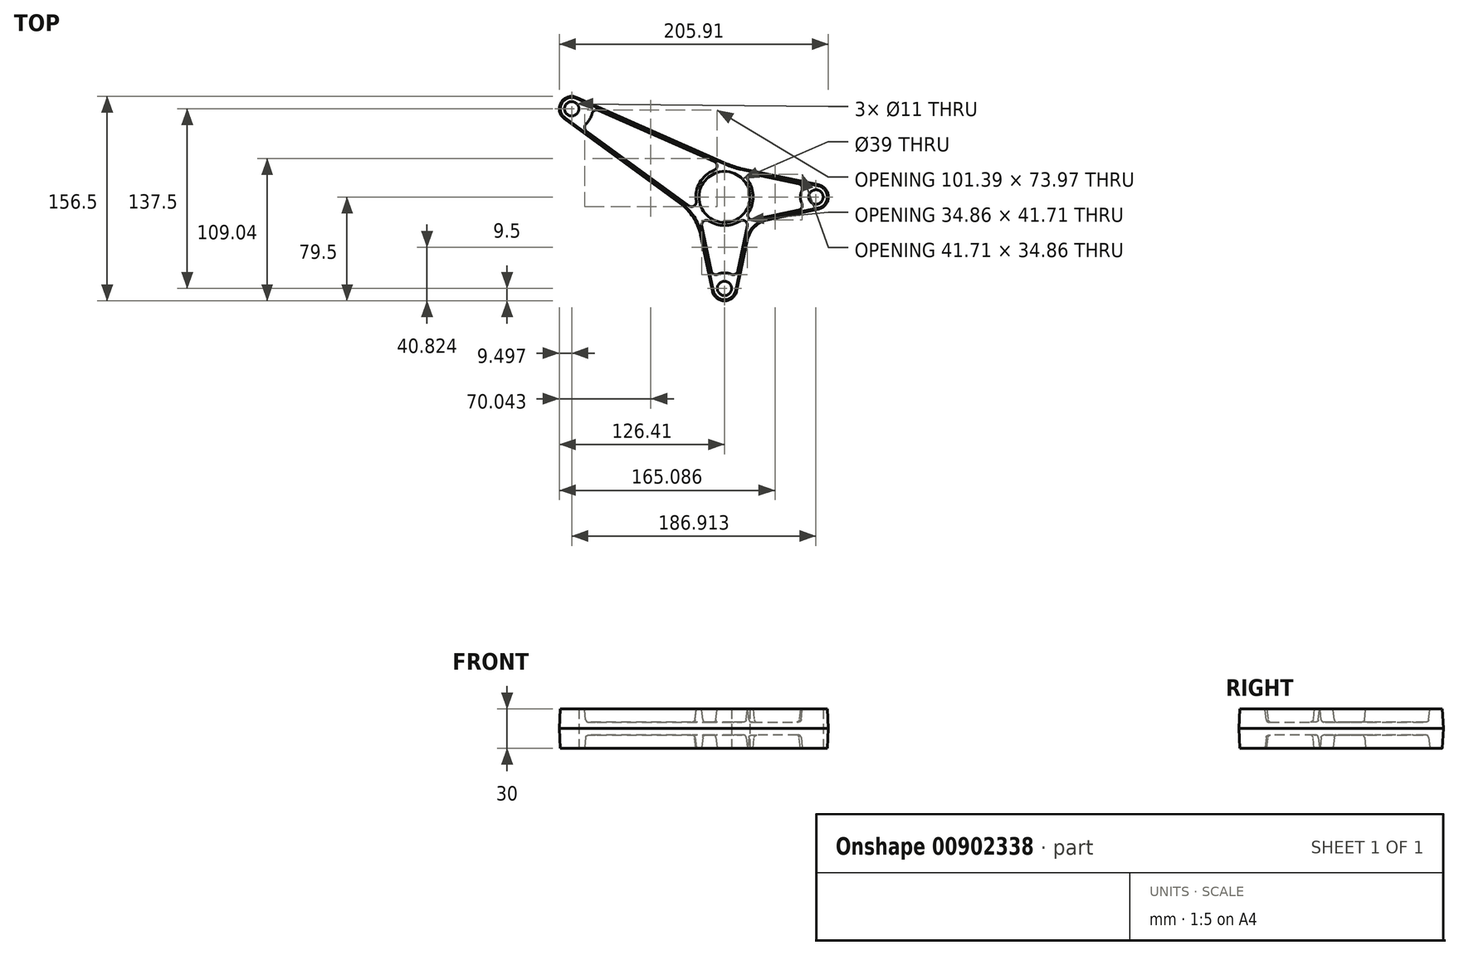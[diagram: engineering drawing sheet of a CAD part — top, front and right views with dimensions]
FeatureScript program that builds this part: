
annotation { "Feature Type Name" : "Feature", "Feature Type Description" : "" }
export const myFeature = defineFeature(function(context is Context, id is Id, definition is map)
    precondition{}
    {
        {
            var Q0;
            Q0=qCreatedBy(makeId("Top.planeOp"),FACE);
            var sketch = newSketch(context, id + "F0", { "sketchPlane" : qUnion([Q0])});
            skLineSegment(sketch, "E0", {"start": v(0, 0) * mm, "end": v(-133.76, 77.23) * mm, "construction": true});
            skLineSegment(sketch, "E1", {"start": v(0, 0) * mm, "end": v(0, -139.43) * mm, "construction": true});
            skCircle(sketch, "E2", {"center": v(0, 0) * mm, "radius": 19.5 * mm});
            skLineSegment(sketch, "E3", {"start": v(0, 0) * mm, "end": v(94.38, 0) * mm, "construction": true});
            skArc(sketch, "E4", {"start": v(0, -70) * mm, "mid": v(49.5, -49.5) * mm, "end": v(70, 0) * mm, "construction": true});
            skCircle(sketch, "E5", {"center": v(0, -70) * mm, "radius": 5.5 * mm});
            skArc(sketch, "E6", {"start": v(-9.3, -71.97) * mm, "mid": v(0, -79.5) * mm, "end": v(9.3, -71.97) * mm});
            skCircle(sketch, "E7", {"center": v(70, 0) * mm, "radius": 5.5 * mm});
            skArc(sketch, "E8", {"start": v(71.97, -9.3) * mm, "mid": v(79.5, 0) * mm, "end": v(71.97, 9.3) * mm});
            skLineSegment(sketch, "E9", {"start": v(71.97, -9.3) * mm, "end": v(32.97, -17.55) * mm});
            skLineSegment(sketch, "E10", {"start": v(9.3, -71.97) * mm, "end": v(17.55, -32.97) * mm});
            skArc(sketch, "E11.trimOffspring", {"start": v(32.97, -17.55) * mm, "mid": v(22.97, -22.97) * mm, "end": v(17.55, -32.97) * mm});
            skArc(sketch, "E12", {"start": v(57.77, 5.7) * mm, "mid": v(56.5, 0) * mm, "end": v(57.77, -5.7) * mm});
            skArc(sketch, "E13", {"start": v(5.7, -57.77) * mm, "mid": v(0, -56.5) * mm, "end": v(-5.7, -57.77) * mm});
            skArc(sketch, "E14", {"start": v(-113.07, 76.19) * mm, "mid": v(-125.14, 72.25) * mm, "end": v(-122.52, 59.83) * mm});
            skCircle(sketch, "E15", {"center": v(-116.91, 67.5) * mm, "radius": 5.5 * mm});
            skArc(sketch, "E16", {"start": v(-18.4, -28.93) * mm, "mid": v(-23.95, -15.5) * mm, "end": v(-33.93, -4.92) * mm});
            skLineSegment(sketch, "E17", {"start": v(-9.3, -71.97) * mm, "end": v(-18.4, -28.93) * mm});
            skLineSegment(sketch, "E18", {"start": v(-122.52, 59.83) * mm, "end": v(-33.93, -4.92) * mm});
            skArc(sketch, "E19", {"start": v(2.66, 25.06) * mm, "mid": v(7.5, 23.22) * mm, "end": v(12.5, 21.88) * mm});
            skLineSegment(sketch, "E20", {"start": v(71.97, 9.3) * mm, "end": v(12.5, 21.88) * mm});
            skLineSegment(sketch, "E21", {"start": v(-113.07, 76.19) * mm, "end": v(2.66, 25.06) * mm});
            skLineSegment(sketch, "E22.0", {"start": v(56.37, 8.5) * mm, "end": v(21.81, 15.82) * mm});
            skLineSegment(sketch, "E23.0", {"start": v(56.37, -8.5) * mm, "end": v(21.81, -15.82) * mm});
            skArc(sketch, "E24.0", {"start": v(19.72, -12.78) * mm, "mid": v(23.5, 0) * mm, "end": v(19.72, 12.78) * mm});
            skArc(sketch, "E25.filletArc", {"start": v(57.77, 5.7) * mm, "mid": v(57.74, 7.44) * mm, "end": v(56.37, 8.5) * mm});
            skArc(sketch, "E26.filletArc", {"start": v(56.37, -8.5) * mm, "mid": v(57.74, -7.44) * mm, "end": v(57.77, -5.7) * mm});
            skArc(sketch, "E27.filletArc", {"start": v(19.72, -12.78) * mm, "mid": v(19.75, -15) * mm, "end": v(21.81, -15.82) * mm});
            skArc(sketch, "E28.trimOffspring", {"start": v(-12.78, -19.72) * mm, "mid": v(0, -23.5) * mm, "end": v(12.78, -19.72) * mm});
            skArc(sketch, "E29.filletArc", {"start": v(21.81, 15.82) * mm, "mid": v(19.75, 15) * mm, "end": v(19.72, 12.78) * mm});
            skArc(sketch, "E30.filletArc", {"start": v(15.82, -21.81) * mm, "mid": v(15, -19.75) * mm, "end": v(12.78, -19.72) * mm});
            skLineSegment(sketch, "E31.trimOffspring", {"start": v(8.5, -56.37) * mm, "end": v(15.82, -21.81) * mm});
            skPoint(sketch, "E32.visualSharp", {"position": v(7.93, -59.08) * mm});
            skArc(sketch, "E32.filletArc", {"start": v(5.7, -57.77) * mm, "mid": v(7.44, -57.74) * mm, "end": v(8.5, -56.37) * mm});
            skLineSegment(sketch, "E33.0", {"start": v(-8.5, -56.37) * mm, "end": v(-15.82, -21.81) * mm});
            skArc(sketch, "E34.filletArc", {"start": v(-12.78, -19.72) * mm, "mid": v(-15, -19.75) * mm, "end": v(-15.82, -21.81) * mm});
            skPoint(sketch, "E35.visualSharp", {"position": v(-7.93, -59.08) * mm});
            skArc(sketch, "E35.filletArc", {"start": v(-8.5, -56.37) * mm, "mid": v(-7.44, -57.74) * mm, "end": v(-5.7, -57.77) * mm});
            skArc(sketch, "E36.trimOffspring", {"start": v(-116.91, 67.5) * mm, "mid": v(-116.91, -67.5) * mm, "end": v(0, -135) * mm, "construction": true});
            skLineSegment(sketch, "E37.0", {"start": v(-97.14, 64.78) * mm, "end": v(-8.44, 25.6) * mm});
            skArc(sketch, "E38.0", {"start": v(-104.87, 54.8) * mm, "mid": v(-101.76, 58.75) * mm, "end": v(-99.9, 63.42) * mm});
            skArc(sketch, "E39.0", {"start": v(-8.52, 21.9) * mm, "mid": v(-20.35, 11.75) * mm, "end": v(-23.23, -3.57) * mm});
            skLineSegment(sketch, "E40.trimOffspring", {"start": v(-104.67, 51.74) * mm, "end": v(-26.38, -5.49) * mm});
            skPoint(sketch, "E41.visualSharp", {"position": v(-99.5, 65.82) * mm});
            skArc(sketch, "E41.filletArc", {"start": v(-97.14, 64.78) * mm, "mid": v(-98.84, 64.74) * mm, "end": v(-99.9, 63.42) * mm});
            skPoint(sketch, "E42.visualSharp", {"position": v(-106.75, 53.26) * mm});
            skArc(sketch, "E42.filletArc", {"start": v(-104.87, 54.8) * mm, "mid": v(-105.49, 53.23) * mm, "end": v(-104.67, 51.74) * mm});
            skPoint(sketch, "E43.visualSharp", {"position": v(-21.76, -8.86) * mm});
            skArc(sketch, "E43.filletArc", {"start": v(-26.38, -5.49) * mm, "mid": v(-24.17, -5.58) * mm, "end": v(-23.23, -3.57) * mm});
            skPoint(sketch, "E44.visualSharp", {"position": v(-3.2, 23.28) * mm});
            skArc(sketch, "E44.filletArc", {"start": v(-8.52, 21.9) * mm, "mid": v(-7.25, 23.72) * mm, "end": v(-8.44, 25.6) * mm});
            skSolve(sketch);
        }
        {
            var Q0;
            Q0=makeQuery(id+"F0.imprint","IMPRINT",FACE,{"disambiguationData":[TD([[makeQuery(id+"F0.imprint","IMPRINT",EDGE,{"derivedFrom":sQuery(id+"F0.wireOp",EDGE,"E2")}),-1.0]])]});
            var Q1;
            Q1=makeQuery(id+"F0.imprint","IMPRINT",FACE,{"disambiguationData":[TD([[makeQuery(id+"F0.imprint","IMPRINT",EDGE,{"derivedFrom":sQuery(id+"F0.wireOp",EDGE,"E13")}),-1.0]])]});
            var Q2;
            Q2=makeQuery(id+"F0.imprint","IMPRINT",FACE,{"disambiguationData":[TD([[makeQuery(id+"F0.imprint","IMPRINT",EDGE,{"derivedFrom":sQuery(id+"F0.wireOp",EDGE,"E15")}),1.0]])]});
            var Q3;
            Q3=makeQuery(id+"F0.imprint","IMPRINT",FACE,{"disambiguationData":[TD([[makeQuery(id+"F0.imprint","IMPRINT",EDGE,{"derivedFrom":sQuery(id+"F0.wireOp",EDGE,"E37.0")}),-1.0]])]});
            var Q4;
            Q4=makeQuery(id+"F0.imprint","IMPRINT",FACE,{"disambiguationData":[TD([[makeQuery(id+"F0.imprint","IMPRINT",EDGE,{"derivedFrom":sQuery(id+"F0.wireOp",EDGE,"E2")}),1.0]])]});
            var Q5;
            Q5=makeQuery(id+"F0.imprint","IMPRINT",FACE,{"disambiguationData":[TD([[makeQuery(id+"F0.imprint","IMPRINT",EDGE,{"derivedFrom":sQuery(id+"F0.wireOp",EDGE,"E5")}),1.0]])]});
            var Q6;
            Q6=makeQuery(id+"F0.imprint","IMPRINT",FACE,{"disambiguationData":[TD([[makeQuery(id+"F0.imprint","IMPRINT",EDGE,{"derivedFrom":sQuery(id+"F0.wireOp",EDGE,"E12")}),-1.0]])]});
            var Q7;
            Q7=makeQuery(id+"F0.imprint","IMPRINT",FACE,{"disambiguationData":[TD([[makeQuery(id+"F0.imprint","IMPRINT",EDGE,{"derivedFrom":sQuery(id+"F0.wireOp",EDGE,"E7")}),1.0]])]});
            extrude(context, id + "F1", {"entities" : qUnion([Q0, Q1, Q2, Q3, Q4, Q5, Q6, Q7]), "depth" : 15 * mm, "offsetDistance" : 25 * mm, "hasDraft" : true, "draftAngle" : 3 * degree, "draftPullDirection" : true});
        }
        {
            var Q0;
            Q0=makeQuery(id+"F0.imprint","IMPRINT",FACE,{"disambiguationData":[TD([[makeQuery(id+"F0.imprint","IMPRINT",EDGE,{"derivedFrom":sQuery(id+"F0.wireOp",EDGE,"E37.0")}),-1.0]])]});
            var Q1;
            Q1=makeQuery(id+"F0.imprint","IMPRINT",FACE,{"disambiguationData":[TD([[makeQuery(id+"F0.imprint","IMPRINT",EDGE,{"derivedFrom":sQuery(id+"F0.wireOp",EDGE,"E13")}),-1.0]])]});
            var Q2;
            Q2=makeQuery(id+"F0.imprint","IMPRINT",FACE,{"disambiguationData":[TD([[makeQuery(id+"F0.imprint","IMPRINT",EDGE,{"derivedFrom":sQuery(id+"F0.wireOp",EDGE,"E12")}),-1.0]])]});
            extrude(context, id + "F2", {"entities" : qUnion([Q0, Q1, Q2]), "operationType" : NewBodyOperationType.REMOVE, "depth" : 30000 * mm, "offsetDistance" : 25 * mm, "hasDraft" : true, "draftAngle" : 6 * degree, "hasSecondDirection" : true, "secondDirectionOppositeDirection" : true, "secondDirectionDepth" : -5 * mm});
        }
        {
            var Q0;
            Q0=makeQuery(id+"F0.imprint","IMPRINT",FACE,{"disambiguationData":[TD([[makeQuery(id+"F0.imprint","IMPRINT",EDGE,{"derivedFrom":sQuery(id+"F0.wireOp",EDGE,"E15")}),1.0]])]});
            var Q1;
            Q1=makeQuery(id+"F0.imprint","IMPRINT",FACE,{"disambiguationData":[TD([[makeQuery(id+"F0.imprint","IMPRINT",EDGE,{"derivedFrom":sQuery(id+"F0.wireOp",EDGE,"E5")}),1.0]])]});
            var Q2;
            Q2=makeQuery(id+"F0.imprint","IMPRINT",FACE,{"disambiguationData":[TD([[makeQuery(id+"F0.imprint","IMPRINT",EDGE,{"derivedFrom":sQuery(id+"F0.wireOp",EDGE,"E2")}),1.0]])]});
            var Q3;
            Q3=makeQuery(id+"F0.imprint","IMPRINT",FACE,{"disambiguationData":[TD([[makeQuery(id+"F0.imprint","IMPRINT",EDGE,{"derivedFrom":sQuery(id+"F0.wireOp",EDGE,"E7")}),1.0]])]});
            var Q4;
            Q4=makeQuery(id+"F1.opExtrude","CAP_FACE",FACE,{"disambiguationData":[OSD([sQuery(id+"F0.wireOp",EDGE,"E6"),sQuery(id+"F0.wireOp",EDGE,"E8"),sQuery(id+"F0.wireOp",EDGE,"E9"),sQuery(id+"F0.wireOp",EDGE,"E10"),sQuery(id+"F0.wireOp",EDGE,"E11.trimOffspring"),sQuery(id+"F0.wireOp",EDGE,"E14"),sQuery(id+"F0.wireOp",EDGE,"E16"),sQuery(id+"F0.wireOp",EDGE,"E17"),sQuery(id+"F0.wireOp",EDGE,"E18"),sQuery(id+"F0.wireOp",EDGE,"E19"),sQuery(id+"F0.wireOp",EDGE,"E20"),sQuery(id+"F0.wireOp",EDGE,"E21")])],"isStart":false});
            extrude(context, id + "F3", {"entities" : qUnion([Q0, Q1, Q2, Q3]), "operationType" : NewBodyOperationType.REMOVE, "endBound" : BoundingType.UP_TO_SURFACE, "depth" : 25 * mm, "endBoundEntityFace" : qUnion([Q4]), "offsetDistance" : 25 * mm});
        }
        {
            var Q0;
            Q0=makeQuery(id+"F2.boolean.opBoolean","COPY",EDGE,{"derivedFrom":makeQuery(id+"F2.opExtrude","CAP_EDGE",EDGE,{"disambiguationData":[OSD([sQuery(id+"F0.wireOp",EDGE,"E37.0")])],"isStart":true})});
            var Q1;
            Q1=makeQuery(id+"F2.boolean.opBoolean","COPY",EDGE,{"derivedFrom":makeQuery(id+"F2.opExtrude","CAP_EDGE",EDGE,{"disambiguationData":[OSD([sQuery(id+"F0.wireOp",EDGE,"E22.0")])],"isStart":true})});
            var Q2;
            Q2=makeQuery(id+"F2.boolean.opBoolean","COPY",EDGE,{"derivedFrom":makeQuery(id+"F2.opExtrude","CAP_EDGE",EDGE,{"disambiguationData":[OSD([sQuery(id+"F0.wireOp",EDGE,"E28.trimOffspring")])],"isStart":true})});
            fillet(context, id + "F4", {"entities" : qUnion([Q0, Q1, Q2]), "radius" : 2 * mm, "tangentPropagation" : true, "allowEdgeOverflow" : false});
        }
        {
            var Q0;
            Q0=makeQuery(id+"F1.opExtrude","SWEPT_BODY",BODY,{"disambiguationData":[OSD([sQuery(id+"F0.wireOp",EDGE,"E6"),sQuery(id+"F0.wireOp",EDGE,"E8"),sQuery(id+"F0.wireOp",EDGE,"E9"),sQuery(id+"F0.wireOp",EDGE,"E10"),sQuery(id+"F0.wireOp",EDGE,"E11.trimOffspring"),sQuery(id+"F0.wireOp",EDGE,"E14"),sQuery(id+"F0.wireOp",EDGE,"E16"),sQuery(id+"F0.wireOp",EDGE,"E17"),sQuery(id+"F0.wireOp",EDGE,"E18"),sQuery(id+"F0.wireOp",EDGE,"E19"),sQuery(id+"F0.wireOp",EDGE,"E20"),sQuery(id+"F0.wireOp",EDGE,"E21")])]});
            var Q1;
            Q1=qCreatedBy(makeId("Top.planeOp"),FACE);
            mirror(context, id + "F5", {"operationType" : NewBodyOperationType.ADD, "entities" : qUnion([Q0]), "mirrorPlane" : qUnion([Q1])});
        }
        {
            var Q0;
            Q0=qCreatedBy(makeId("Top.planeOp"),FACE);
            var sketch = newSketch(context, id + "F6", { "sketchPlane" : qUnion([Q0])});
            skLineSegment(sketch, "E45.0", {"start": v(-17.04, -2) * mm, "end": v(17.04, -2) * mm});
            skArc(sketch, "E46.filletArc", {"start": v(-17.04, -2) * mm, "mid": v(-18.6, -2.76) * mm, "end": v(-18.98, -4.46) * mm});
            skArc(sketch, "E47.filletArc", {"start": v(18.98, -4.46) * mm, "mid": v(18.6, -2.76) * mm, "end": v(17.04, -2) * mm});
            skArc(sketch, "E48.MirrorCS", {"start": v(18.98, 4.46) * mm, "mid": v(18.6, 2.76) * mm, "end": v(17.04, 2) * mm});
            skArc(sketch, "E49.MirrorCS", {"start": v(-17.04, 2) * mm, "mid": v(-18.6, 2.76) * mm, "end": v(-18.98, 4.46) * mm});
            skLineSegment(sketch, "E50", {"start": v(-17.04, 2) * mm, "end": v(17.04, 2) * mm});
            skPoint(sketch, "E51.0.center.orphan", {"position": v(0, 0) * mm});
            skArc(sketch, "E52.0", {"start": v(-18.98, 4.46) * mm, "mid": v(-19.5, 0) * mm, "end": v(-18.98, -4.46) * mm});
            skArc(sketch, "E53.trimOffspring", {"start": v(18.98, -4.46) * mm, "mid": v(19.5, 0) * mm, "end": v(18.98, 4.46) * mm});
            skPoint(sketch, "E54.orphan", {"position": v(-19.5, 0) * mm});
            skSolve(sketch);
        }
    });
